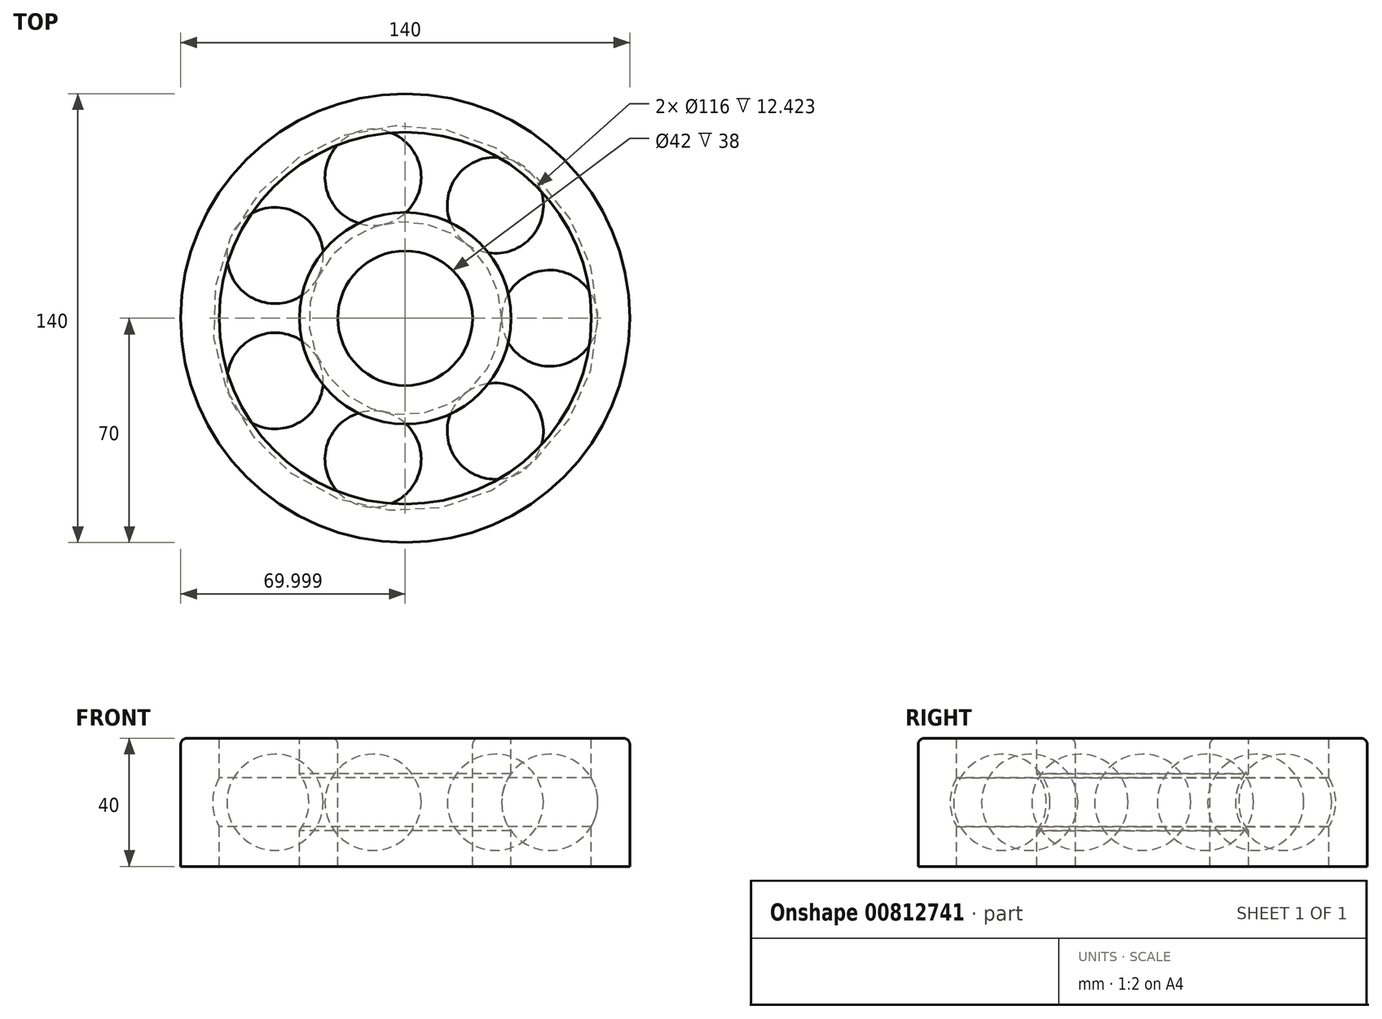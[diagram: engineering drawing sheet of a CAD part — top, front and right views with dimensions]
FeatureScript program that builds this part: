
annotation { "Feature Type Name" : "Feature", "Feature Type Description" : "" }
export const myFeature = defineFeature(function(context is Context, id is Id, definition is map)
    precondition{}
    {
        {
            var Q0;
            Q0=qCreatedBy(makeId("Front.planeOp"),FACE);
            var sketch = newSketch(context, id + "F0", { "sketchPlane" : qUnion([Q0])});
            skLineSegment(sketch, "E0.bottom", {"start": v(21.3, 16.46) * mm, "end": v(33.3, 16.46) * mm});
            skLineSegment(sketch, "E0.top", {"start": v(21.3, -23.54) * mm, "end": v(33.3, -23.54) * mm});
            skLineSegment(sketch, "E0.left", {"start": v(21.3, 16.46) * mm, "end": v(21.3, -23.54) * mm});
            skLineSegment(sketch, "E0.right", {"start": v(33.3, 16.46) * mm, "end": v(33.3, -23.54) * mm});
            skLineSegment(sketch, "E1.bottom", {"start": v(58.3, 16.46) * mm, "end": v(70.3, 16.46) * mm});
            skLineSegment(sketch, "E1.top", {"start": v(58.3, -23.54) * mm, "end": v(70.3, -23.54) * mm});
            skLineSegment(sketch, "E1.left", {"start": v(58.3, 16.46) * mm, "end": v(58.3, -23.54) * mm});
            skLineSegment(sketch, "E1.right", {"start": v(70.3, 16.46) * mm, "end": v(70.3, -23.54) * mm});
            skLineSegment(sketch, "E2", {"start": v(11.34, -3.54) * mm, "end": v(79.39, -3.54) * mm});
            skCircle(sketch, "E3", {"center": v(45.36, -3.54) * mm, "radius": 15 * mm});
            skLineSegment(sketch, "E4", {"start": v(0.3, 28.58) * mm, "end": v(0.3, -41.64) * mm});
            skSolve(sketch);
        }
        {
            var Q0;
            {var subQ0=sQuery(id+"F0.wireOp",EDGE,"E3");var subQ1=sQuery(id+"F0.wireOp",EDGE,"E0.right");var subQ2=makeQuery(id+"F0.imprint","INTERSECT",VERTEX,{"disambiguationData":[OD(0.0)],"derivedFrom":[subQ1,subQ0]});Q0=makeQuery(id+"F0.imprint","IMPRINT",FACE,{"disambiguationData":[TD([[makeQuery(id+"F0.imprint","IMPRINT",EDGE,{"disambiguationData":[TD([[subQ2,-1.0]])],"derivedFrom":subQ1}),1.0]])]});}
            var Q1;
            {var subQ0=sQuery(id+"F0.wireOp",EDGE,"E3");var subQ1=sQuery(id+"F0.wireOp",EDGE,"E0.right");var subQ2=makeQuery(id+"F0.imprint","INTERSECT",VERTEX,{"disambiguationData":[OD(0.0)],"derivedFrom":[subQ1,subQ0]});Q1=makeQuery(id+"F0.imprint","IMPRINT",FACE,{"disambiguationData":[TD([[makeQuery(id+"F0.imprint","IMPRINT",EDGE,{"disambiguationData":[TD([[subQ2,-1.0]])],"derivedFrom":subQ1}),-1.0]])]});}
            var Q2;
            {var subQ0=sQuery(id+"F0.wireOp",EDGE,"E3");var subQ1=sQuery(id+"F0.wireOp",EDGE,"E1.left");var subQ2=makeQuery(id+"F0.imprint","INTERSECT",VERTEX,{"disambiguationData":[OD(0.0)],"derivedFrom":[subQ1,subQ0]});Q2=makeQuery(id+"F0.imprint","IMPRINT",FACE,{"disambiguationData":[TD([[makeQuery(id+"F0.imprint","IMPRINT",EDGE,{"disambiguationData":[TD([[subQ2,-1.0]])],"derivedFrom":subQ1}),1.0]])]});}
            var Q3;
            Q3=sQuery(id+"F0.wireOp",EDGE,"E2");
            revolve(context, id + "F1", {"surfaceOperationType" : NewSurfaceOperationType.NEW, "entities" : qUnion([Q0, Q1, Q2]), "axis" : qUnion([Q3]), "revolveType" : RevolveType.FULL});
        }
        {
            var Q0;
            {var subQ6=sQuery(id+"F0.wireOp",EDGE,"E0.bottom");Q0=makeQuery(id+"F0.imprint","IMPRINT",FACE,{"disambiguationData":[TD([[makeQuery(id+"F0.imprint","IMPRINT",EDGE,{"derivedFrom":subQ6}),-1.0]])]});}
            var Q1;
            {var subQ1=sQuery(id+"F0.wireOp",EDGE,"E1.bottom");Q1=makeQuery(id+"F0.imprint","IMPRINT",FACE,{"disambiguationData":[TD([[makeQuery(id+"F0.imprint","IMPRINT",EDGE,{"derivedFrom":subQ1}),-1.0]])]});}
            var Q2;
            {var subQ5=sQuery(id+"F0.wireOp",EDGE,"E1.top");Q2=makeQuery(id+"F0.imprint","IMPRINT",FACE,{"disambiguationData":[TD([[makeQuery(id+"F0.imprint","IMPRINT",EDGE,{"derivedFrom":subQ5}),1.0]])]});}
            var Q3;
            {var subQ1=sQuery(id+"F0.wireOp",EDGE,"E0.top");Q3=makeQuery(id+"F0.imprint","IMPRINT",FACE,{"disambiguationData":[TD([[makeQuery(id+"F0.imprint","IMPRINT",EDGE,{"derivedFrom":subQ1}),1.0]])]});}
            var Q4;
            Q4=sQuery(id+"F0.wireOp",EDGE,"E4");
            revolve(context, id + "F2", {"surfaceOperationType" : NewSurfaceOperationType.NEW, "entities" : qUnion([Q0, Q1, Q2, Q3]), "axis" : qUnion([Q4]), "revolveType" : RevolveType.FULL});
        }
        {
            var Q0;
            Q0=makeQuery(id+"F1.opRevolve","SWEPT_BODY",BODY,{"disambiguationData":[OSD([sQuery(id+"F0.wireOp",EDGE,"E2"),sQuery(id+"F0.wireOp",EDGE,"E3")])]});
            var Q1;
            Q1=makeQuery(id+"F2.opRevolve","SWEPT_FACE",FACE,{"disambiguationData":[OSD([sQuery(id+"F0.wireOp",EDGE,"E0.left")])]});
            circularPattern(context, id + "F3", {"entities" : qUnion([Q0]), "axis" : qUnion([Q1]), "angle" : 360 * degree, "instanceCount" : 7, "equalSpace" : true});
        }
        {
            var Q0;
            Q0=makeQuery(id+"F2.opRevolve","SWEPT_EDGE",EDGE,{"disambiguationData":[OSD([sQuery(id+"F0.wireOp",EDGE,"E0.bottom"),sQuery(id+"F0.wireOp",EDGE,"E0.left")])]});
            fillet(context, id + "F4", {"entities" : qUnion([Q0]), "radius" : 2 * mm, "tangentPropagation" : true, "allowEdgeOverflow" : false});
        }
        {
            var Q0;
            Q0=makeQuery(id+"F2.opRevolve","SWEPT_EDGE",EDGE,{"disambiguationData":[OSD([sQuery(id+"F0.wireOp",EDGE,"E1.bottom"),sQuery(id+"F0.wireOp",EDGE,"E1.right")])]});
            fillet(context, id + "F5", {"entities" : qUnion([Q0]), "radius" : 2 * mm, "tangentPropagation" : true, "allowEdgeOverflow" : false});
        }
    });
